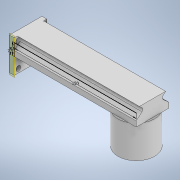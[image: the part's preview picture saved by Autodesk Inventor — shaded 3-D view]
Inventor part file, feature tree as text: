
AUTODESK INVENTOR PART (.ipt)
format: ipt  version: 2021.1 (Build 251245010, 245A)  size: 176,128 bytes
history: native  units: mm
features: sketch x6, extrude x5, plane x4, mirror x2
ambient origin geometry x8: Origin, YZ Plane, XZ Plane, XY Plane, X Axis, Y Axis, Z Axis, Center Point
bodies: Solid1 (feature_tree)
feature tree (17):
  extrude  "Extrusion1"  Depth=40.0mm
  extrude  "Extrusion2"  Depth=5.0mm
  mirror  "Mirror1"
  mirror  "Mirror2"
  plane  "Work Plane4"
  sketch  "Sketch3"  dims[d5=5.0mm d6=6.0mm]
  extrude  "Extrusion3"  Depth=6.0mm
  extrude  "Extrusion4"  [1 undecoded]
  extrude  "Extrusion5"  Depth=150.0mm
  sketch  "Sketch1"  dims[d0=40.0mm d1=40.0mm]
  sketch  "Sketch2"  dims[d2=6.0mm d3=0.0mm d4=5.0mm]
  plane  "Work Plane1"
  plane  "Work Plane2"
  plane  "Work Plane3"
  sketch  "Sketch4"  dims[d7=6.0mm d8=0.0mm d9=-20.0mm]
  sketch  "Sketch5"  dims[d10=15.0mm d11=150.0mm]
  sketch  "Sketch6"  dims[d12=7.5mm d13=150.0mm d14=0.0mm d15=10.0mm d16=60.0mm d17=40.0mm d18=45.0mm d19=40.0mm d20=0.0mm d21=38.0mm d22=25.0mm d23=0.0mm]
note: 1 required parameter value undecoded (feature->parameter linkage not recoverable at this tier; creation-order binding heuristic only, values carry confidence <= 0.55)
